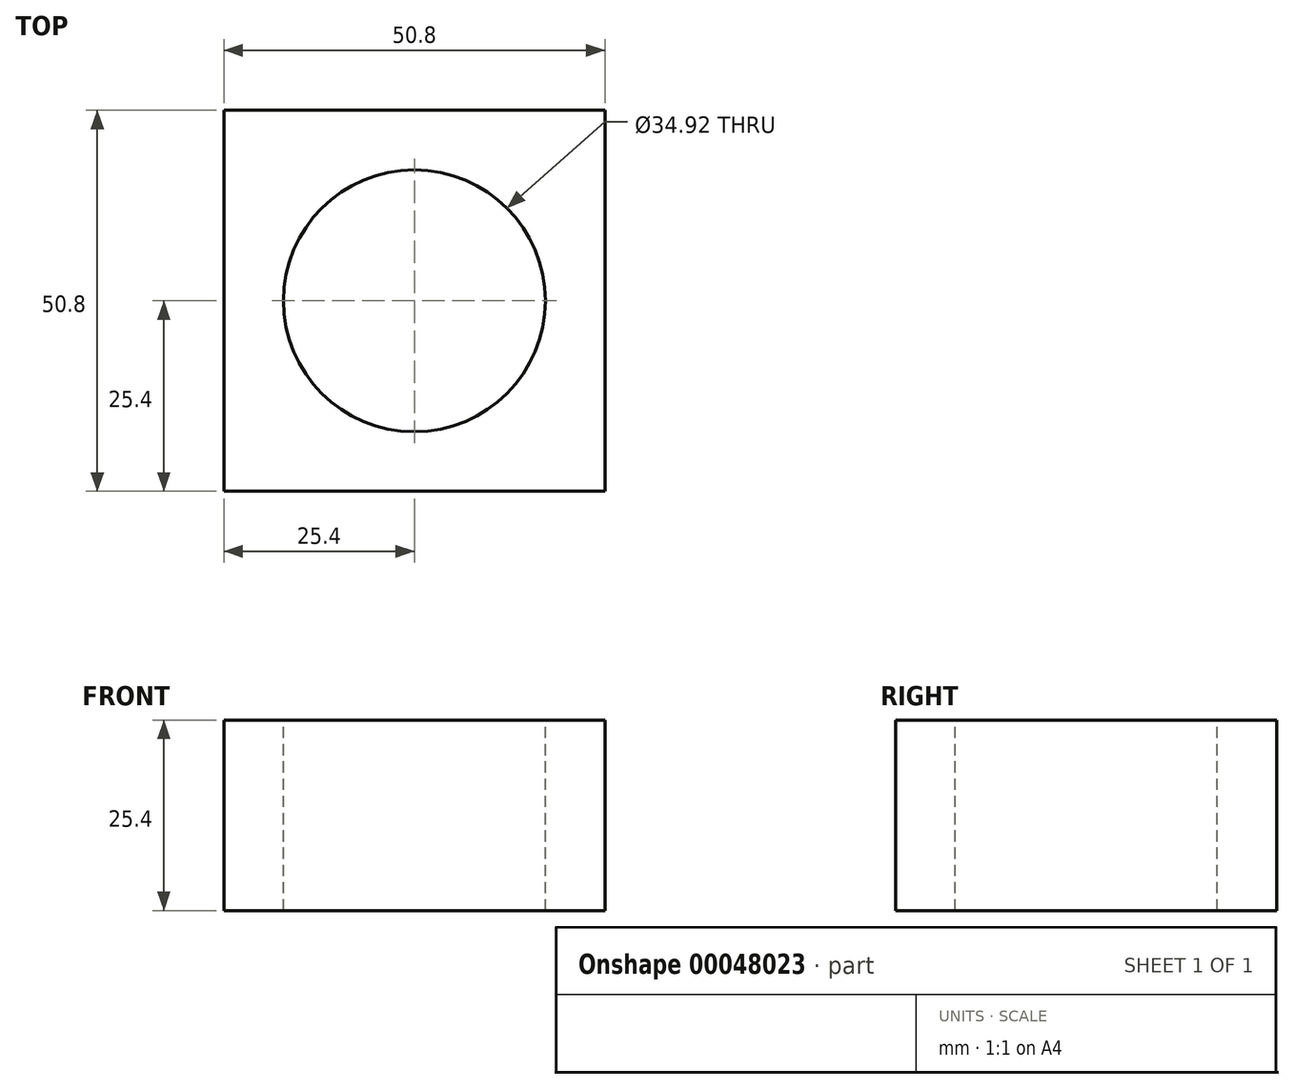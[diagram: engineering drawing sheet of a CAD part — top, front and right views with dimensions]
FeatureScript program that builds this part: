
annotation { "Feature Type Name" : "Feature", "Feature Type Description" : "" }
export const myFeature = defineFeature(function(context is Context, id is Id, definition is map)
    precondition{}
    {
        {
            var Q0;
            Q0=qCreatedBy(makeId("Top.planeOp"),FACE);
            var sketch = newSketch(context, id + "F0", { "sketchPlane" : qUnion([Q0])});
            skLineSegment(sketch, "E0.bottom", {"start": v(-25.4, 25.4) * mm, "end": v(25.4, 25.4) * mm});
            skLineSegment(sketch, "E0.top", {"start": v(-25.4, -25.4) * mm, "end": v(25.4, -25.4) * mm});
            skLineSegment(sketch, "E0.left", {"start": v(-25.4, 25.4) * mm, "end": v(-25.4, -25.4) * mm});
            skLineSegment(sketch, "E0.right", {"start": v(25.4, 25.4) * mm, "end": v(25.4, -25.4) * mm});
            skLineSegment(sketch, "E1", {"start": v(0, 25.4) * mm, "end": v(0, 0) * mm, "construction": true});
            skLineSegment(sketch, "E2", {"start": v(0, 0) * mm, "end": v(-25.4, 0) * mm, "construction": true});
            skSolve(sketch);
        }
        {
            var Q0;
            Q0=makeQuery(id+"F0.imprint","IMPRINT",FACE,{"disambiguationData":[TD([[makeQuery(id+"F0.imprint","IMPRINT",EDGE,{"derivedFrom":sQuery(id+"F0.wireOp",EDGE,"E0.bottom")}),-1.0]])]});
            extrude(context, id + "F1", {"entities" : qUnion([Q0]), "endBound" : BoundingType.SYMMETRIC, "depth" : 25.4 * mm});
        }
        {
            var Q0;
            Q0=makeQuery(id+"F1.opExtrude","CAP_FACE",FACE,{"disambiguationData":[OSD([sQuery(id+"F0.wireOp",EDGE,"E0.bottom"),sQuery(id+"F0.wireOp",EDGE,"E0.top"),sQuery(id+"F0.wireOp",EDGE,"E0.left"),sQuery(id+"F0.wireOp",EDGE,"E0.right")])],"isStart":false});
            var sketch = newSketch(context, id + "F2", { "sketchPlane" : qUnion([Q0])});
            skCircle(sketch, "E3", {"center": v(0, 0) * mm, "radius": 17.46 * mm});
            skSolve(sketch);
        }
        {
            var Q0;
            Q0=makeQuery(id+"F2.imprint","IMPRINT",FACE,{"disambiguationData":[TD([[makeQuery(id+"F2.imprint","IMPRINT",EDGE,{"derivedFrom":sQuery(id+"F2.wireOp",EDGE,"E3")}),-1.0]])]});
            var Q1;
            Q1=makeQuery(id+"F1.opExtrude","CAP_FACE",FACE,{"disambiguationData":[OSD([sQuery(id+"F0.wireOp",EDGE,"E0.bottom"),sQuery(id+"F0.wireOp",EDGE,"E0.top"),sQuery(id+"F0.wireOp",EDGE,"E0.left"),sQuery(id+"F0.wireOp",EDGE,"E0.right")])],"isStart":true});
            extrude(context, id + "F3", {"entities" : qUnion([Q0]), "operationType" : NewBodyOperationType.INTERSECT, "endBound" : BoundingType.UP_TO_SURFACE, "oppositeDirection" : true, "endBoundEntityFace" : qUnion([Q1]), "depth" : 25.4 * mm});
        }
    });
